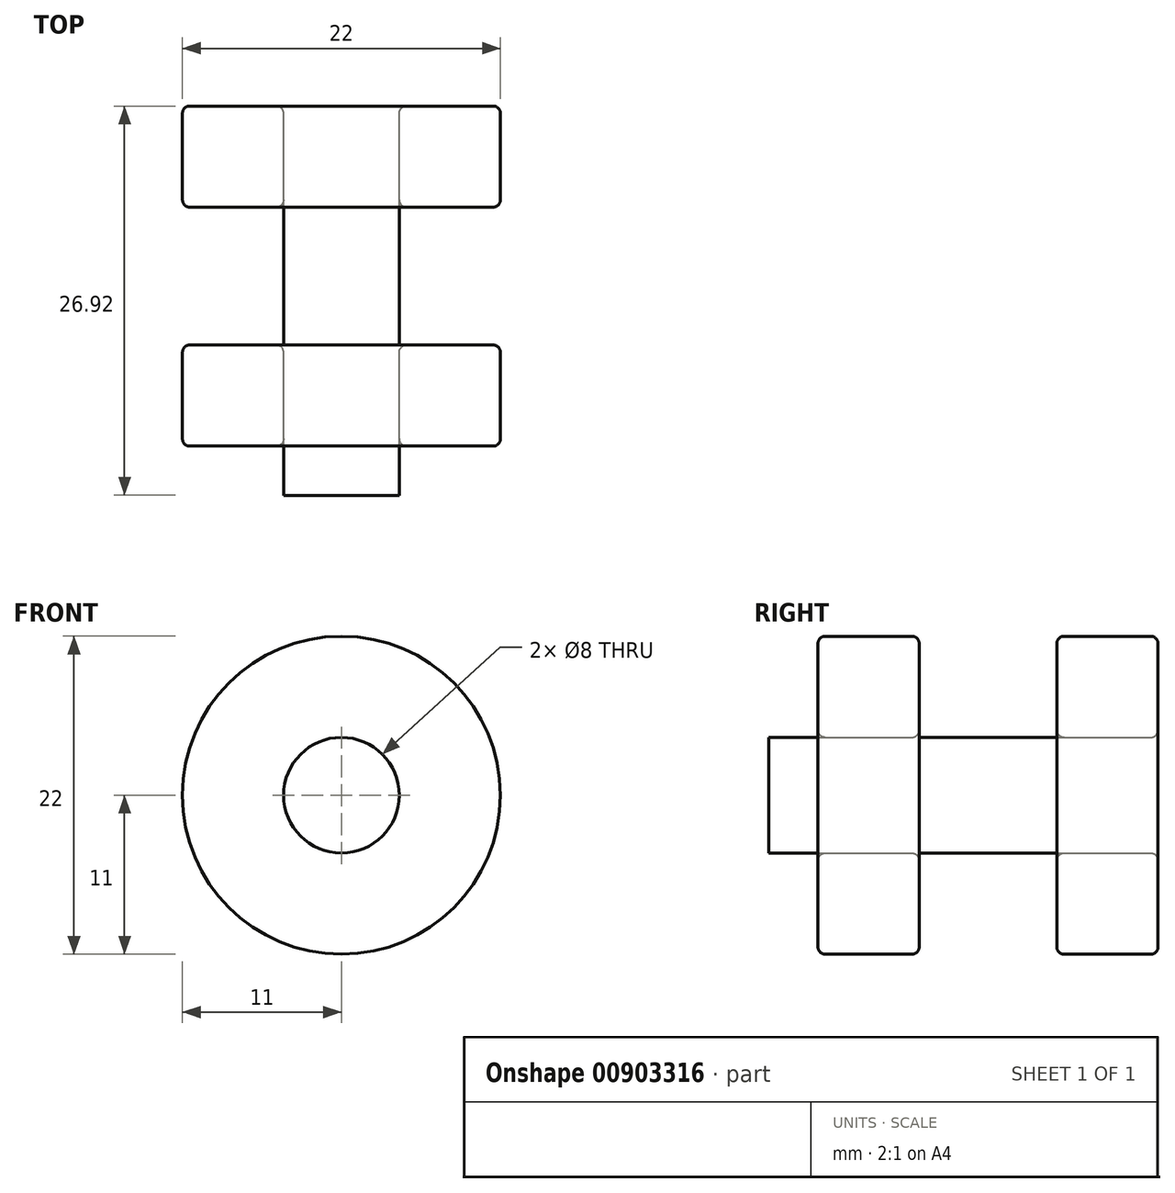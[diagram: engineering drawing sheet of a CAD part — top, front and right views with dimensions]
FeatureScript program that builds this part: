
annotation { "Feature Type Name" : "Feature", "Feature Type Description" : "" }
export const myFeature = defineFeature(function(context is Context, id is Id, definition is map)
    precondition{}
    {
        {
            var Q0;
            Q0=qCreatedBy(makeId("Front.planeOp"),FACE);
            var sketch = newSketch(context, id + "F0", { "sketchPlane" : qUnion([Q0])});
            skCircle(sketch, "E0", {"center": v(0, 0) * mm, "radius": 4 * mm});
            skCircle(sketch, "E1", {"center": v(0, 0) * mm, "radius": 11 * mm});
            skSolve(sketch);
        }
        {
            var Q0;
            Q0=makeQuery(id+"F0.imprint","IMPRINT",FACE,{"disambiguationData":[TD([[makeQuery(id+"F0.imprint","IMPRINT",EDGE,{"derivedFrom":sQuery(id+"F0.wireOp",EDGE,"E0")}),-1.0]])]});
            extrude(context, id + "F1", {"entities" : qUnion([Q0]), "depth" : 7 * mm, "offsetDistance" : 25.4 * mm});
        }
        {
            var Q0;
            Q0=makeQuery(id+"F1.opExtrude","CAP_EDGE",EDGE,{"disambiguationData":[OSD([sQuery(id+"F0.wireOp",EDGE,"E1")])],"isStart":false});
            var Q1;
            Q1=makeQuery(id+"F1.opExtrude","CAP_EDGE",EDGE,{"disambiguationData":[OSD([sQuery(id+"F0.wireOp",EDGE,"E1")])],"isStart":true});
            var Q2;
            Q2=makeQuery(id+"F1.opExtrude","CAP_EDGE",EDGE,{"disambiguationData":[OSD([sQuery(id+"F0.wireOp",EDGE,"E0")])],"isStart":true});
            var Q3;
            Q3=makeQuery(id+"F1.opExtrude","CAP_EDGE",EDGE,{"disambiguationData":[OSD([sQuery(id+"F0.wireOp",EDGE,"E0")])],"isStart":false});
            fillet(context, id + "F2", {"entities" : qUnion([Q0, Q1, Q2, Q3]), "radius" : 0.5 * mm, "tangentPropagation" : true, "allowEdgeOverflow" : false});
        }
        {
            var Q0;
            Q0=makeQuery(id+"F1.opExtrude","CAP_FACE",FACE,{"disambiguationData":[OSD([sQuery(id+"F0.wireOp",EDGE,"E0"),sQuery(id+"F0.wireOp",EDGE,"E1")])],"isStart":false});
            cPlane(context, id + "F3", {"entities" : qUnion([Q0]), "cplaneType" : CPlaneType.OFFSET, "offset" : 9.52 * mm, "width" : 152.4 * mm, "height" : 152.4 * mm});
        }
        {
            var Q0;
            Q0=qCreatedBy(id+"F3.planeOp",FACE);
            var sketch = newSketch(context, id + "F4", { "sketchPlane" : qUnion([Q0])});
            skCircle(sketch, "E2", {"center": v(0, 0) * mm, "radius": 4 * mm});
            skCircle(sketch, "E3", {"center": v(0, 0) * mm, "radius": 11 * mm});
            skSolve(sketch);
        }
        {
            var Q0;
            Q0 = qSketchRegion(id + "F4", true);
            extrude(context, id + "F5", {"entities" : qUnion([Q0]), "depth" : 7 * mm, "offsetDistance" : 25.4 * mm});
        }
        {
            var Q0;
            Q0=makeQuery(id+"F5.opExtrude","CAP_EDGE",EDGE,{"disambiguationData":[OSD([sQuery(id+"F4.wireOp",EDGE,"E3")])],"isStart":false});
            var Q1;
            Q1=makeQuery(id+"F5.opExtrude","CAP_EDGE",EDGE,{"disambiguationData":[OSD([sQuery(id+"F4.wireOp",EDGE,"E3")])],"isStart":true});
            var Q2;
            Q2=makeQuery(id+"F5.opExtrude","CAP_EDGE",EDGE,{"disambiguationData":[OSD([sQuery(id+"F4.wireOp",EDGE,"E2")])],"isStart":false});
            var Q3;
            Q3=makeQuery(id+"F5.opExtrude","CAP_EDGE",EDGE,{"disambiguationData":[OSD([sQuery(id+"F4.wireOp",EDGE,"E2")])],"isStart":true});
            fillet(context, id + "F6", {"entities" : qUnion([Q0, Q1, Q2, Q3]), "radius" : 0.5 * mm, "tangentPropagation" : true, "allowEdgeOverflow" : false});
        }
        {
            var Q0;
            Q0=makeQuery(id+"F0.imprint","IMPRINT",FACE,{"disambiguationData":[TD([[makeQuery(id+"F0.imprint","IMPRINT",EDGE,{"derivedFrom":sQuery(id+"F0.wireOp",EDGE,"E0")}),1.0]])]});
            var Q1;
            Q1=makeQuery(id+"F5.opExtrude","SWEPT_BODY",BODY,{"disambiguationData":[OSD([sQuery(id+"F4.wireOp",EDGE,"E2"),sQuery(id+"F4.wireOp",EDGE,"E3")])]});
            extrude(context, id + "F7", {"entities" : qUnion([Q0]), "depth" : 26.92 * mm, "endBoundEntityBody" : qUnion([Q1]), "offsetDistance" : 25.4 * mm});
        }
    });
